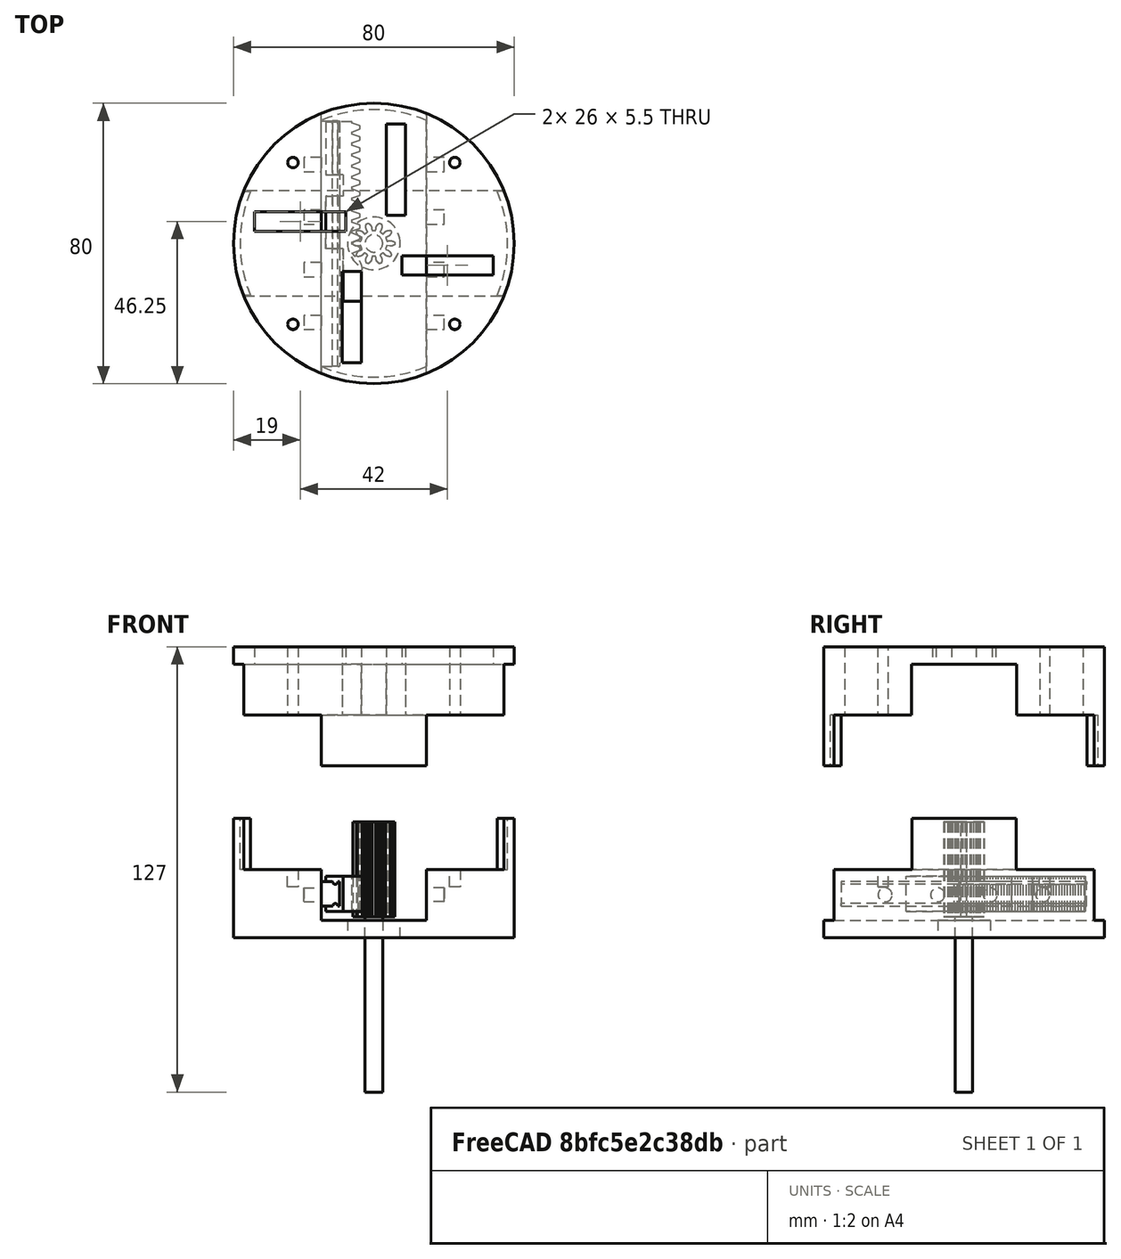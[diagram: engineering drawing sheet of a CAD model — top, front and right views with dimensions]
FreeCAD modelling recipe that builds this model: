
FCSTD DOCUMENT  (FreeCAD 1.1R20260414 (Git shallow))
Label: 2+2Jaw
License: All rights reserved
LicenseURL: https://en.wikipedia.org/wiki/All_rights_reserved
objects: Sketcher::SketchObject×17, PartDesign::Pocket×11, App::Link×7, App::Point×6, PartDesign::Pad×6, PartDesign::Body×5, Part::DatumPlane×2, PartDesign::FeaturePython×2, App::FeaturePython×1, Assembly::JointGroup×1, Assembly::AssemblyObject×1
note: 94 computed .brp shape members not serialized (recipe doc carries the construction recipe); baked Part::Feature solids carry a one-line shape summary decoded from their .brp

FEATURE [App::Point] Origin001
  Role = Origin
FEATURE [App::Point] Origin005  label="Origin006"
  Role = Origin
FEATURE [Sketcher::SketchObject] Sketch
  ArcFitTolerance = 1e-06
  AttachmentSupport = -> [Origin004]
  ExternalTypes = [0]
  FullyConstrained = true
  MakeInternals = false
  MapMode = 5
  _ExternalGeoVersion = 1
  sketch-geometry (2):
    g0: Circle CenterX=0 CenterY=0 CenterZ=0 NormalX=0 NormalY=0 NormalZ=1 AngleXU=0 Radius=40
    g1: Circle CenterX=0 CenterY=0 CenterZ=0 NormalX=0 NormalY=0 NormalZ=1 AngleXU=0 Radius=7.5
  constraints (4):
    c: Diameter(g0) = 80
    c: Coincident(g0,g-1)
    c: Diameter(g1) = 15
    c: Coincident(g1,g0)
FEATURE [PartDesign::Pad] Pad
  Direction = (0,0,1)
  Length = 34
  Length2 = 10
  Profile = -> Sketch
  ReferenceAxis = -> Sketch [N_Axis]
  Refine = true
  SideType = 0
  Suppressed = false
  Type = 0
  Type2 = 0
FEATURE [Part::DatumPlane] DatumPlane
  AttachmentSupport = -> [Origin004]
  MapMode = 5
  Placement = pos=(0,0,0) rot=(1,0,0;1.5708rad)
FEATURE [Sketcher::SketchObject] Sketch001
  ArcFitTolerance = 1e-06
  AttachmentSupport = -> [DatumPlane]
  ExternalGeometry = -> [Pad]
  ExternalTypes = [0,0,0]
  FullyConstrained = true
  MakeInternals = false
  MapMode = 5
  Placement = pos=(0,0,0) rot=(1,0,0;1.5708rad)
  _ExternalGeoVersion = 1
  sketch-geometry (5):
    g0: LineSegment StartX=-15 StartY=34 StartZ=0 EndX=-15 EndY=5 EndZ=0
    g1: LineSegment StartX=-15 StartY=5 StartZ=0 EndX=15 EndY=5 EndZ=0
    g2: LineSegment StartX=15 StartY=5 StartZ=0 EndX=15 EndY=34 EndZ=0
    g3: LineSegment StartX=-15 StartY=34 StartZ=0 EndX=0 EndY=34 EndZ=0
    g4: LineSegment StartX=0 StartY=34 StartZ=0 EndX=15 EndY=34 EndZ=0
  constraints (15):
    c: Coincident(g0,g1)
    c: Coincident(g1,g2)
    c: Vertical(g0)
    c: Vertical(g2)
    c: Horizontal(g1)
    c: Distance(g1,g-4) = 5
    c: Coincident(g0,g3)
    c: Horizontal(g3)
    c: Coincident(g3,g4)
    c: Horizontal(g4)
    c: PointOnObject(g3,g-2)
    c: Coincident(g4,g2)
    c: Equal(g3,g4)
    c: PointOnObject(g0,g-3)
    c: DistanceX(g1,g1) = 30
FEATURE [PartDesign::Pocket] Pocket
  BaseFeature = -> Pad
  Direction = (0,1,-2e-16)
  Length = 5
  Length2 = 5
  Profile = -> Sketch001
  ReferenceAxis = -> Sketch001 [N_Axis]
  Refine = true
  SideType = 2
  Suppressed = false
  Type = 1
  Type2 = 0
FEATURE [Sketcher::SketchObject] Sketch002
  ArcFitTolerance = 1e-06
  AttachmentSupport = -> [Pocket]
  ExternalGeometry = -> [Pocket]
  ExternalTypes = [0,0,0]
  FullyConstrained = true
  MakeInternals = false
  MapMode = 5
  Placement = pos=(0,0,34) rot=(0,0,1;0rad)
  _ExternalGeoVersion = 1
  sketch-geometry (16):
    g0: LineSegment StartX=35.1413 StartY=-14.85 StartZ=0 EndX=37.1413 EndY=-14.85 EndZ=0
    g1: LineSegment StartX=37.1413 StartY=14.85 StartZ=0 EndX=35.1413 EndY=14.85 EndZ=0
    g2: LineSegment [constr] StartX=37.1413 StartY=-14.85 StartZ=0 EndX=37.1413 EndY=0 EndZ=0
    g3: LineSegment [constr] StartX=37.1413 StartY=0 StartZ=0 EndX=37.1413 EndY=14.85 EndZ=0
    g4: ArcOfCircle CenterX=0 CenterY=0 CenterZ=0 NormalX=0 NormalY=0 NormalZ=1 AngleXU=0 Radius=38.1502 StartAngle=5.88337 EndAngle=6.683
    g5: LineSegment StartX=-35.1413 StartY=-14.85 StartZ=0 EndX=-37.1413 EndY=-14.85 EndZ=0
    g6: LineSegment StartX=-37.1413 StartY=14.85 StartZ=0 EndX=-35.1413 EndY=14.85 EndZ=0
    g7: LineSegment [constr] StartX=-37.1413 StartY=-14.85 StartZ=0 EndX=-37.1413 EndY=0 EndZ=0
    g8: LineSegment [constr] StartX=-37.1413 StartY=0 StartZ=0 EndX=-37.1413 EndY=14.85 EndZ=0
    g9: ArcOfCircle CenterX=0 CenterY=0 CenterZ=0 NormalX=0 NormalY=0 NormalZ=1 AngleXU=0 Radius=38.1502 StartAngle=2.74177 EndAngle=3.54141
    g10: LineSegment StartX=-37.1413 StartY=14.85 StartZ=0 EndX=-37.1413 EndY=40 EndZ=0
    g11: LineSegment StartX=-37.1413 StartY=40 StartZ=0 EndX=37.1413 EndY=40 EndZ=0
    g12: LineSegment StartX=-37.1413 StartY=-14.85 StartZ=0 EndX=-37.1413 EndY=-40 EndZ=0
    g13: LineSegment StartX=-37.1413 StartY=-40 StartZ=0 EndX=37.1413 EndY=-40 EndZ=0
    g14: LineSegment StartX=37.1413 StartY=-40 StartZ=0 EndX=37.1413 EndY=-14.85 EndZ=0
    g15: LineSegment StartX=37.1413 StartY=14.85 StartZ=0 EndX=37.1413 EndY=40 EndZ=0
  constraints (46):
    c: Horizontal(g0)
    c: Horizontal(g1)
    c: Coincident(g2,g0)
    c: PointOnObject(g2,g-1)
    c: Vertical(g2)
    c: Coincident(g3,g2)
    c: Coincident(g3,g1)
    c: Vertical(g3)
    c: Equal(g2,g3)
    c: PointOnObject(g1,g-3)
    c: Coincident(g4,g-3)
    c: Coincident(g4,g0)
    c: Coincident(g4,g1)
    c: Distance(g1,g1) = 2
    c: Horizontal(g5)
    c: Horizontal(g6)
    c: Coincident(g7,g5)
    c: Vertical(g7)
    c: Coincident(g8,g7)
    c: Coincident(g8,g6)
    c: Vertical(g8)
    c: Equal(g7,g8)
    c: Coincident(g9,g5)
    c: Coincident(g9,g6)
    c: Coincident(g9,g4)
    c: PointOnObject(g7,g-1)
    c: PointOnObject(g5,g-3)
    c: Equal(g7,g2)
    c: Distance(g5,g6) = 29.7
    c: Coincident(g6,g10)
    c: Vertical(g10)
    c: Coincident(g10,g11)
    c: Horizontal(g11)
    c: Coincident(g5,g12)
    c: Vertical(g12)
    c: Coincident(g12,g13)
    c: Horizontal(g13)
    c: Coincident(g13,g14)
    c: Coincident(g14,g0)
    c: Vertical(g14)
    c: Coincident(g15,g1)
    c: Coincident(g15,g11)
    c: Vertical(g15)
    c: Tangent(g13,g-3)
    c: Equal(g6,g1)
    c: Tangent(g11,g-3)
FEATURE [PartDesign::Pocket] Pocket001
  BaseFeature = -> Pocket
  Direction = (0,0,-1)
  Length = 14.5
  Length2 = 5
  Profile = -> Sketch002
  ReferenceAxis = -> Sketch002 [N_Axis]
  Refine = true
  SideType = 0
  Suppressed = false
  Type = 0
  Type2 = 0
FEATURE [Sketcher::SketchObject] Sketch003
  ArcFitTolerance = 1e-06
  AttachmentSupport = -> [Pocket001]
  ExternalGeometry = -> [Pocket001]
  ExternalTypes = [0,0,0,0]
  FullyConstrained = true
  MakeInternals = false
  MapMode = 5
  Placement = pos=(0,0,19.5) rot=(0,0,1;0rad)
  _ExternalGeoVersion = 1
  sketch-geometry (20):
    g0: Circle CenterX=-23.0923 CenterY=22.9991 CenterZ=0 NormalX=0 NormalY=0 NormalZ=1 AngleXU=0 Radius=1.5
    g1: ArcOfCircle [constr] CenterX=-45.3233 CenterY=45.1404 CenterZ=0 NormalX=0 NormalY=0 NormalZ=1 AngleXU=0 Radius=31.376 StartAngle=4.97621 EndAngle=6.02341
    g2: LineSegment [constr] StartX=-37.1413 StartY=14.85 StartZ=0 EndX=-23.0923 EndY=22.9991 EndZ=0
    g3: LineSegment [constr] StartX=-23.0923 StartY=22.9991 StartZ=0 EndX=-15 EndY=37.081 EndZ=0
    g4: LineSegment [constr] StartX=-37.1413 StartY=14.85 StartZ=0 EndX=-15 EndY=37.081 EndZ=0
    g5: ArcOfCircle [constr] CenterX=45.3233 CenterY=45.1404 CenterZ=0 NormalX=0 NormalY=0 NormalZ=1 AngleXU=0 Radius=31.376 StartAngle=3.40137 EndAngle=4.44857
    g6: ArcOfCircle [constr] CenterX=-45.3233 CenterY=-45.1404 CenterZ=0 NormalX=0 NormalY=0 NormalZ=1 AngleXU=0 Radius=31.376 StartAngle=0.259778 EndAngle=1.30698
    g7: ArcOfCircle [constr] CenterX=45.3233 CenterY=-45.1404 CenterZ=0 NormalX=0 NormalY=0 NormalZ=1 AngleXU=0 Radius=31.376 StartAngle=1.83462 EndAngle=2.88181
    g8: LineSegment [constr] StartX=-37.1413 StartY=-14.85 StartZ=0 EndX=-23.0923 EndY=-22.9991 EndZ=0
    g9: LineSegment [constr] StartX=-23.0923 StartY=-22.9991 StartZ=0 EndX=-15 EndY=-37.081 EndZ=0
    g10: LineSegment [constr] StartX=-15 StartY=-37.081 StartZ=0 EndX=-37.1413 EndY=-14.85 EndZ=0
    g11: LineSegment [constr] StartX=15 StartY=-37.081 StartZ=0 EndX=37.1413 EndY=-14.85 EndZ=0
    g12: LineSegment [constr] StartX=37.1413 StartY=-14.85 StartZ=0 EndX=23.0923 EndY=-22.9991 EndZ=0
    g13: LineSegment [constr] StartX=23.0923 StartY=-22.9991 StartZ=0 EndX=15 EndY=-37.081 EndZ=0
    g14: LineSegment [constr] StartX=15 StartY=37.081 StartZ=0 EndX=23.0923 EndY=22.9991 EndZ=0
    g15: LineSegment [constr] StartX=23.0923 StartY=22.9991 StartZ=0 EndX=37.1413 EndY=14.85 EndZ=0
    g16: LineSegment [constr] StartX=37.1413 StartY=14.85 StartZ=0 EndX=15 EndY=37.081 EndZ=0
    g17: Circle CenterX=23.0923 CenterY=22.9991 CenterZ=0 NormalX=0 NormalY=0 NormalZ=1 AngleXU=0 Radius=1.5
    g18: Circle CenterX=23.0923 CenterY=-22.9991 CenterZ=0 NormalX=0 NormalY=0 NormalZ=1 AngleXU=0 Radius=1.5
    g19: Circle CenterX=-23.0923 CenterY=-22.9991 CenterZ=0 NormalX=0 NormalY=0 NormalZ=1 AngleXU=0 Radius=1.5
  constraints (48):
    c: Diameter(g0) = 3
    c: Coincident(g1,g-6)
    c: Coincident(g1,g-6)
    c: PointOnObject(g0,g1)
    c: Coincident(g1,g2)
    c: Coincident(g2,g3)
    c: Coincident(g3,g1)
    c: Equal(g3,g2)
    c: Coincident(g2,g0)
    c: Coincident(g4,g1)
    c: Coincident(g4,g1)
    c: Angle(g2,g4) = 0.261799
    c: Coincident(g5,g-3)
    c: Coincident(g5,g-3)
    c: Coincident(g6,g-5)
    c: Coincident(g6,g-5)
    c: Coincident(g7,g-4)
    c: Coincident(g7,g-4)
    c: Coincident(g6,g8)
    c: Coincident(g8,g9)
    c: Coincident(g9,g6)
    c: Coincident(g9,g10)
    c: Coincident(g10,g8)
    c: Coincident(g7,g11)
    c: Coincident(g11,g12)
    c: Coincident(g12,g13)
    c: Coincident(g13,g11)
    c: Coincident(g5,g14)
    c: Coincident(g14,g15)
    c: Coincident(g15,g5)
    c: Coincident(g15,g16)
    c: Coincident(g16,g14)
    c: Equal(g8,g9)
    c: Equal(g15,g14)
    c: Equal(g12,g13)
    c: PointOnObject(g8,g6)
    c: PointOnObject(g12,g7)
    c: Coincident(g11,g7)
    c: PointOnObject(g14,g5)
    c: Angle(g10,g8) = 0.261799
    c: Angle(g12,g11) = 0.261799
    c: Angle(g16,g15) = 0.261799
    c: Coincident(g17,g14)
    c: Coincident(g18,g12)
    c: Coincident(g19,g8)
    c: Equal(g0,g17)
    c: Equal(g0,g19)
    c: Equal(g0,g18)
FEATURE [PartDesign::Pocket] Pocket002
  BaseFeature = -> Pocket001
  Direction = (0,0,-1)
  Length = 5
  Length2 = 5
  Profile = -> Sketch003
  ReferenceAxis = -> Sketch003 [N_Axis]
  Refine = true
  SideType = 0
  Suppressed = false
  Type = 0
  Type2 = 0
FEATURE [Part::DatumPlane] DatumPlane001
  AttachmentSupport = -> [Origin006]
  MapMode = 5
  Placement = pos=(0,0,0) rot=(1,0,0;1.5708rad)
FEATURE [App::Point] Origin007  label="Origin009"
  Role = Origin
FEATURE [Sketcher::SketchObject] Sketch004
  ArcFitTolerance = 1e-06
  AttachmentSupport = -> [Origin006]
  ExternalTypes = [0]
  FullyConstrained = true
  MakeInternals = false
  MapMode = 5
  _ExternalGeoVersion = 1
  sketch-geometry (1):
    g0: Circle CenterX=0 CenterY=0 CenterZ=0 NormalX=0 NormalY=0 NormalZ=1 AngleXU=0 Radius=40
  constraints (2):
    c: Diameter(g0) = 80
    c: Coincident(g0,g-1)
FEATURE [PartDesign::Pad] Pad001
  Direction = (0,0,1)
  Length = 34
  Length2 = 10
  Profile = -> Sketch004
  ReferenceAxis = -> Sketch004 [N_Axis]
  Refine = true
  SideType = 0
  Suppressed = false
  Type = 0
  Type2 = 0
FEATURE [Sketcher::SketchObject] Sketch005
  ArcFitTolerance = 1e-06
  AttachmentSupport = -> [DatumPlane001]
  ExternalGeometry = -> [Pad001]
  ExternalTypes = [0,0,0]
  FullyConstrained = true
  MakeInternals = false
  MapMode = 5
  Placement = pos=(0,0,0) rot=(1,0,0;1.5708rad)
  _ExternalGeoVersion = 1
  sketch-geometry (5):
    g0: LineSegment StartX=-15 StartY=34 StartZ=0 EndX=-15 EndY=5 EndZ=0
    g1: LineSegment StartX=-15 StartY=5 StartZ=0 EndX=15 EndY=5 EndZ=0
    g2: LineSegment StartX=15 StartY=5 StartZ=0 EndX=15 EndY=34 EndZ=0
    g3: LineSegment StartX=-15 StartY=34 StartZ=0 EndX=0 EndY=34 EndZ=0
    g4: LineSegment StartX=0 StartY=34 StartZ=0 EndX=15 EndY=34 EndZ=0
  constraints (15):
    c: Coincident(g0,g1)
    c: Coincident(g1,g2)
    c: Vertical(g0)
    c: Vertical(g2)
    c: Horizontal(g1)
    c: Distance(g1,g-4) = 5
    c: Coincident(g0,g3)
    c: Horizontal(g3)
    c: Coincident(g3,g4)
    c: Horizontal(g4)
    c: PointOnObject(g3,g-2)
    c: Coincident(g4,g2)
    c: Equal(g3,g4)
    c: PointOnObject(g0,g-3)
    c: DistanceX(g1,g1) = 30
FEATURE [PartDesign::Pocket] Pocket003
  BaseFeature = -> Pad001
  Direction = (0,1,-2e-16)
  Length = 5
  Length2 = 5
  Profile = -> Sketch005
  ReferenceAxis = -> Sketch005 [N_Axis]
  Refine = true
  SideType = 2
  Suppressed = false
  Type = 1
  Type2 = 0
FEATURE [Sketcher::SketchObject] Sketch006
  ArcFitTolerance = 1e-06
  AttachmentSupport = -> [Pocket003]
  ExternalGeometry = -> [Pocket003]
  ExternalTypes = [0,0,0]
  FullyConstrained = true
  MakeInternals = false
  MapMode = 5
  Placement = pos=(0,0,34) rot=(0,0,1;0rad)
  _ExternalGeoVersion = 1
  sketch-geometry (16):
    g0: LineSegment StartX=35.081 StartY=-15 StartZ=0 EndX=37.081 EndY=-15 EndZ=0
    g1: LineSegment StartX=37.081 StartY=15 StartZ=0 EndX=35.081 EndY=15 EndZ=0
    g2: LineSegment [constr] StartX=37.081 StartY=-15 StartZ=0 EndX=37.081 EndY=0 EndZ=0
    g3: LineSegment [constr] StartX=37.081 StartY=0 StartZ=0 EndX=37.081 EndY=15 EndZ=0
    g4: ArcOfCircle CenterX=0 CenterY=0 CenterZ=0 NormalX=0 NormalY=0 NormalZ=1 AngleXU=0 Radius=38.1533 StartAngle=5.87913 EndAngle=6.68724
    g5: LineSegment StartX=-35.081 StartY=-15 StartZ=0 EndX=-37.081 EndY=-15 EndZ=0
    g6: LineSegment StartX=-37.081 StartY=15 StartZ=0 EndX=-35.081 EndY=15 EndZ=0
    g7: LineSegment [constr] StartX=-37.081 StartY=-15 StartZ=0 EndX=-37.081 EndY=0 EndZ=0
    g8: LineSegment [constr] StartX=-37.081 StartY=0 StartZ=0 EndX=-37.081 EndY=15 EndZ=0
    g9: ArcOfCircle CenterX=0 CenterY=0 CenterZ=0 NormalX=0 NormalY=0 NormalZ=1 AngleXU=0 Radius=38.1533 StartAngle=2.73754 EndAngle=3.54565
    g10: LineSegment StartX=-37.081 StartY=15 StartZ=0 EndX=-37.081 EndY=40 EndZ=0
    g11: LineSegment StartX=-37.081 StartY=40 StartZ=0 EndX=37.081 EndY=40 EndZ=0
    g12: LineSegment StartX=-37.081 StartY=-15 StartZ=0 EndX=-37.081 EndY=-40 EndZ=0
    g13: LineSegment StartX=-37.081 StartY=-40 StartZ=0 EndX=37.081 EndY=-40 EndZ=0
    g14: LineSegment StartX=37.081 StartY=-40 StartZ=0 EndX=37.081 EndY=-15 EndZ=0
    g15: LineSegment StartX=37.081 StartY=15 StartZ=0 EndX=37.081 EndY=40 EndZ=0
  constraints (46):
    c: Horizontal(g0)
    c: Horizontal(g1)
    c: Coincident(g2,g0)
    c: PointOnObject(g2,g-1)
    c: Vertical(g2)
    c: Coincident(g3,g2)
    c: Coincident(g3,g1)
    c: Vertical(g3)
    c: Equal(g2,g3)
    c: PointOnObject(g1,g-3)
    c: Coincident(g4,g-3)
    c: Coincident(g4,g0)
    c: Coincident(g4,g1)
    c: Distance(g1,g1) = 2
    c: Horizontal(g5)
    c: Horizontal(g6)
    c: Coincident(g7,g5)
    c: Vertical(g7)
    c: Coincident(g8,g7)
    c: Coincident(g8,g6)
    c: Vertical(g8)
    c: Equal(g7,g8)
    c: Coincident(g9,g5)
    c: Coincident(g9,g6)
    c: Coincident(g9,g4)
    c: PointOnObject(g7,g-1)
    c: PointOnObject(g5,g-3)
    c: Equal(g7,g2)
    c: Distance(g5,g6) = 30
    c: Coincident(g6,g10)
    c: Vertical(g10)
    c: Coincident(g10,g11)
    c: Horizontal(g11)
    c: Coincident(g5,g12)
    c: Vertical(g12)
    c: Coincident(g12,g13)
    c: Horizontal(g13)
    c: Coincident(g13,g14)
    c: Coincident(g14,g0)
    c: Vertical(g14)
    c: Coincident(g15,g1)
    c: Coincident(g15,g11)
    c: Vertical(g15)
    c: Tangent(g13,g-3)
    c: Equal(g6,g1)
    c: Tangent(g11,g-3)
FEATURE [PartDesign::Pocket] Pocket004
  BaseFeature = -> Pocket003
  Direction = (0,0,-1)
  Length = 14.5
  Length2 = 5
  Profile = -> Sketch006
  ReferenceAxis = -> Sketch006 [N_Axis]
  Refine = true
  SideType = 0
  Suppressed = false
  Type = 0
  Type2 = 0
FEATURE [Sketcher::SketchObject] Sketch007
  ArcFitTolerance = 1e-06
  AttachmentSupport = -> [Pocket004]
  ExternalGeometry = -> [Pocket004]
  ExternalTypes = [0,0,0,0]
  FullyConstrained = true
  MakeInternals = false
  MapMode = 5
  Placement = pos=(0,0,19.5) rot=(0,0,1;0rad)
  _ExternalGeoVersion = 1
  sketch-geometry (20):
    g0: Circle CenterX=-23.0822 CenterY=23.0822 CenterZ=0 NormalX=0 NormalY=0 NormalZ=1 AngleXU=0 Radius=1.5
    g1: ArcOfCircle [constr] CenterX=-45.1632 CenterY=45.1632 CenterZ=0 NormalX=0 NormalY=0 NormalZ=1 AngleXU=0 Radius=31.2272 StartAngle=4.97419 EndAngle=6.02139
    g2: LineSegment [constr] StartX=-37.081 StartY=15 StartZ=0 EndX=-23.0822 EndY=23.0822 EndZ=0
    g3: LineSegment [constr] StartX=-23.0822 StartY=23.0822 StartZ=0 EndX=-15 EndY=37.081 EndZ=0
    g4: LineSegment [constr] StartX=-37.081 StartY=15 StartZ=0 EndX=-15 EndY=37.081 EndZ=0
    g5: ArcOfCircle [constr] CenterX=45.1632 CenterY=45.1632 CenterZ=0 NormalX=0 NormalY=0 NormalZ=1 AngleXU=0 Radius=31.2272 StartAngle=3.40339 EndAngle=4.45059
    g6: ArcOfCircle [constr] CenterX=-45.1632 CenterY=-45.1632 CenterZ=0 NormalX=0 NormalY=0 NormalZ=1 AngleXU=0 Radius=31.2272 StartAngle=0.261799 EndAngle=1.309
    g7: ArcOfCircle [constr] CenterX=45.1632 CenterY=-45.1632 CenterZ=0 NormalX=0 NormalY=0 NormalZ=1 AngleXU=0 Radius=31.2272 StartAngle=1.8326 EndAngle=2.87979
    g8: LineSegment [constr] StartX=-37.081 StartY=-15 StartZ=0 EndX=-23.0822 EndY=-23.0822 EndZ=0
    g9: LineSegment [constr] StartX=-23.0822 StartY=-23.0822 StartZ=0 EndX=-15 EndY=-37.081 EndZ=0
    g10: LineSegment [constr] StartX=-15 StartY=-37.081 StartZ=0 EndX=-37.081 EndY=-15 EndZ=0
    g11: LineSegment [constr] StartX=15 StartY=-37.081 StartZ=0 EndX=37.081 EndY=-15 EndZ=0
    g12: LineSegment [constr] StartX=37.081 StartY=-15 StartZ=0 EndX=23.0822 EndY=-23.0822 EndZ=0
    g13: LineSegment [constr] StartX=23.0822 StartY=-23.0822 StartZ=0 EndX=15 EndY=-37.081 EndZ=0
    g14: LineSegment [constr] StartX=15 StartY=37.081 StartZ=0 EndX=23.0822 EndY=23.0822 EndZ=0
    g15: LineSegment [constr] StartX=23.0822 StartY=23.0822 StartZ=0 EndX=37.081 EndY=15 EndZ=0
    g16: LineSegment [constr] StartX=37.081 StartY=15 StartZ=0 EndX=15 EndY=37.081 EndZ=0
    g17: Circle CenterX=23.0822 CenterY=23.0822 CenterZ=0 NormalX=0 NormalY=0 NormalZ=1 AngleXU=0 Radius=1.5
    g18: Circle CenterX=23.0822 CenterY=-23.0822 CenterZ=0 NormalX=0 NormalY=0 NormalZ=1 AngleXU=0 Radius=1.5
    g19: Circle CenterX=-23.0822 CenterY=-23.0822 CenterZ=0 NormalX=0 NormalY=0 NormalZ=1 AngleXU=0 Radius=1.5
  constraints (48):
    c: Diameter(g0) = 3
    c: Coincident(g1,g-6)
    c: Coincident(g1,g-6)
    c: PointOnObject(g0,g1)
    c: Coincident(g1,g2)
    c: Coincident(g2,g3)
    c: Coincident(g3,g1)
    c: Equal(g3,g2)
    c: Coincident(g2,g0)
    c: Coincident(g4,g1)
    c: Coincident(g4,g1)
    c: Angle(g2,g4) = 0.261799
    c: Coincident(g5,g-3)
    c: Coincident(g5,g-3)
    c: Coincident(g6,g-5)
    c: Coincident(g6,g-5)
    c: Coincident(g7,g-4)
    c: Coincident(g7,g-4)
    c: Coincident(g6,g8)
    c: Coincident(g8,g9)
    c: Coincident(g9,g6)
    c: Coincident(g9,g10)
    c: Coincident(g10,g8)
    c: Coincident(g7,g11)
    c: Coincident(g11,g12)
    c: Coincident(g12,g13)
    c: Coincident(g13,g11)
    c: Coincident(g5,g14)
    c: Coincident(g14,g15)
    c: Coincident(g15,g5)
    c: Coincident(g15,g16)
    c: Coincident(g16,g14)
    c: Equal(g8,g9)
    c: Equal(g15,g14)
    c: Equal(g12,g13)
    c: PointOnObject(g8,g6)
    c: PointOnObject(g12,g7)
    c: Coincident(g11,g7)
    c: PointOnObject(g14,g5)
    c: Angle(g10,g8) = 0.261799
    c: Angle(g12,g11) = 0.261799
    c: Angle(g16,g15) = 0.261799
    c: Coincident(g17,g14)
    c: Coincident(g18,g12)
    c: Coincident(g19,g8)
    c: Equal(g0,g17)
    c: Equal(g0,g19)
    c: Equal(g0,g18)
FEATURE [PartDesign::Pocket] Pocket005
  BaseFeature = -> Pocket004
  Direction = (0,0,-1)
  Length = 5
  Length2 = 5
  Profile = -> Sketch007
  ReferenceAxis = -> Sketch007 [N_Axis]
  Refine = true
  SideType = 0
  Suppressed = false
  Type = 1
  Type2 = 0
FEATURE [App::Point] Origin009  label="Origin011"
  Role = Origin
FEATURE [App::Point] Origin011  label="Origin013"
  Role = Origin
FEATURE [PartDesign::FeaturePython] InvoluteGear  # WARN: FeaturePython — macro-defined, semantics opaque (R4)
  AttacherType = Attacher::AttachEngine3D
  Suppressed = false
  addendum_diameter = 12
  angular_backlash = 0
  axle_hole = false
  axle_holesize = 10
  backlash = 0
  clearance = 0.25
  double_helix = false
  head = 0
  head_fillet = 0
  height = 27
  helix_angle = 0
  module = 1
  num_teeth = 10
  numpoints = 20
  offset_hole = false
  offset_holeoffset = 10
  offset_holesize = 10
  pitch_diameter = 10
  pressure_angle = 20
  properties_from_tool = false
  reversed_backlash = false
  root_diameter = 7.5
  root_fillet = 0
  shift = 0
  simple = false
  transverse_pitch = 3.14159
  traverse_module = 1
  undercut = false
  version = 1.3.0
  expr: angular_backlash = backlash / pitch_diameter * 360 ° / pi
FEATURE [Sketcher::SketchObject] Sketch008
  ArcFitTolerance = 1e-06
  AttachmentSupport = -> [InvoluteGear]
  ExternalTypes = [0]
  FullyConstrained = true
  MakeInternals = false
  MapMode = 5
  Placement = pos=(0,0,27) rot=(0,0,1;0rad)
  _ExternalGeoVersion = 1
  sketch-geometry (1):
    g0: Circle CenterX=0 CenterY=0 CenterZ=0 NormalX=0 NormalY=0 NormalZ=1 AngleXU=0 Radius=2.5
  constraints (2):
    c: Diameter(g0) = 5
    c: Coincident(g0,g-1)
FEATURE [PartDesign::Pad] Pad002
  BaseFeature = -> InvoluteGear
  Direction = (0,0,1)
  Length = 50
  Length2 = 10
  Profile = -> Sketch008
  ReferenceAxis = -> Sketch008 [N_Axis]
  Refine = true
  SideType = 0
  Suppressed = false
  Type = 0
  Type2 = 0
FEATURE [PartDesign::Body] Body003  label="Shaft"
  AllowCompound = false
  Group = -> [InvoluteGear,Sketch008,Pad002]
  Origin = -> Origin010
  Placement = pos=(0,4e-15,33) rot=(1,0,0;3.14159rad)
  Tip = -> Pad002
FEATURE [PartDesign::FeaturePython] InvoluteRack  # WARN: FeaturePython — macro-defined, semantics opaque (R4)
  AttacherType = Attacher::AttachEngine3D
  Suppressed = false
  add_endings = true
  clearance = 0.25
  double_helix = false
  head = 0
  head_fillet = 0
  height = 10
  helix_angle = 0
  module = 1
  num_teeth = 12
  pressure_angle = 20
  properties_from_tool = false
  root_fillet = 0
  simplified = false
  thickness = 1
  transverse_pitch = 3.14159
  version = 1.3.0
FEATURE [Sketcher::SketchObject] Sketch009
  ArcFitTolerance = 1e-06
  AttachmentSupport = -> [InvoluteRack]
  ExternalGeometry = -> [InvoluteRack]
  ExternalTypes = [0,0,0]
  FullyConstrained = true
  MakeInternals = false
  MapMode = 5
  Placement = pos=(0,0,0) rot=(1,0,0;3.14159rad)
  _ExternalGeoVersion = 1
  sketch-geometry (10):
    g0: ArcOfCircle CenterX=2.74624 CenterY=-1.76464 CenterZ=0 NormalX=0 NormalY=0 NormalZ=1 AngleXU=0 Radius=5 StartAngle=2.2143 EndAngle=3.10281
    g1: LineSegment StartX=-3.75 StartY=-36.1283 StartZ=0 EndX=-3.75 EndY=15 EndZ=0
    g2: LineSegment StartX=-3.75 StartY=15 StartZ=0 EndX=1.74624 EndY=15 EndZ=0
    g3: LineSegment StartX=1.74624 StartY=15 StartZ=0 EndX=1.74624 EndY=6.23536 EndZ=0
    g4: ArcOfCircle CenterX=-3.25376 CenterY=6.23536 CenterZ=0 NormalX=0 NormalY=0 NormalZ=1 AngleXU=0 Radius=5 StartAngle=5.35589 EndAngle=6.28319
    g5: LineSegment [constr] StartX=2.74624 StartY=-1.76464 StartZ=0 EndX=2.74624 EndY=15 EndZ=0
    g6: LineSegment [constr] StartX=1.74624 StartY=15 StartZ=0 EndX=2.74624 EndY=15 EndZ=0
    g7: LineSegment [constr] StartX=-2.25 StartY=-1.5708 StartZ=0 EndX=-1.25 EndY=-1.5708 EndZ=0
    g8: LineSegment StartX=-2.25 StartY=-1.5708 StartZ=0 EndX=-2.25 EndY=-36.1283 EndZ=0
    g9: LineSegment StartX=-2.25 StartY=-36.1283 StartZ=0 EndX=-3.75 EndY=-36.1283 EndZ=0
  constraints (27):
    c: Radius(g0) = 5
    c: Vertical(g1)
    c: Coincident(g1,g2)
    c: Horizontal(g2)
    c: Coincident(g2,g3)
    c: Vertical(g3)
    c: Coincident(g5,g0)
    c: Vertical(g5)
    c: Coincident(g6,g2)
    c: Coincident(g6,g5)
    c: Horizontal(g6)
    c: Tangent(g4,g0) = 1.5708
    c: Tangent(g4,g3) = 1.5708
    c: PointOnObject(g-3,g0)
    c: Distance(g-1,g2) = 15
    c: Equal(g4,g0)
    c: Coincident(g7,g0)
    c: Symmetric(g-4,g-4,g7)
    c: Horizontal(g7)
    c: Distance(g3,g5) = 1
    c: Coincident(g8,g0)
    c: Coincident(g8,g-5)
    c: Vertical(g8)
    c: Coincident(g9,g8)
    c: Coincident(g9,g1)
    c: Horizontal(g9)
    c: Distance(g9,g9) = 1.5
FEATURE [App::Point] Origin013  label="Origin016"
  Role = Origin
FEATURE [Sketcher::SketchObject] Sketch012
  ArcFitTolerance = 1e-06
  AttachmentSupport = -> [Origin012]
  ExternalTypes = [0]
  FullyConstrained = true
  MakeInternals = false
  MapMode = 5
  _ExternalGeoVersion = 1
  sketch-geometry (4):
    g0: LineSegment StartX=0 StartY=0 StartZ=0 EndX=70 EndY=0 EndZ=0
    g1: LineSegment StartX=70 StartY=0 StartZ=0 EndX=70 EndY=7 EndZ=0
    g2: LineSegment StartX=70 StartY=7 StartZ=0 EndX=0 EndY=7 EndZ=0
    g3: LineSegment StartX=0 StartY=7 StartZ=0 EndX=0 EndY=0 EndZ=0
  constraints (11):
    c: Coincident(g0,g1)
    c: Coincident(g1,g2)
    c: Coincident(g2,g3)
    c: Coincident(g3,g0)
    c: Horizontal(g0)
    c: Horizontal(g2)
    c: Vertical(g1)
    c: Vertical(g3)
    c: Distance(g1,g3) = 70
    c: Distance(g0,g2) = 7
    c: Coincident(g0,g-1)
FEATURE [PartDesign::Pad] Pad005
  Direction = (0,0,1)
  Length = 5.25
  Length2 = 10
  Profile = -> Sketch012
  ReferenceAxis = -> Sketch012 [N_Axis]
  Refine = true
  SideType = 0
  Suppressed = false
  Type = 0
  Type2 = 0
FEATURE [Sketcher::SketchObject] Sketch013
  ArcFitTolerance = 1e-06
  AttachmentSupport = -> [Pad005]
  ExternalGeometry = -> [Pad005]
  ExternalTypes = [0,0,0]
  FullyConstrained = true
  MakeInternals = false
  MapMode = 5
  Placement = pos=(0,0,0) rot=(0.57735,-0.57735,-0.57735;2.0944rad)
  _ExternalGeoVersion = 1
  sketch-geometry (5):
    g0: LineSegment StartX=-7 StartY=4.75 StartZ=0 EndX=-7 EndY=3.25 EndZ=0
    g1: ArcOfCircle CenterX=-7 CenterY=4 CenterZ=0 NormalX=0 NormalY=0 NormalZ=1 AngleXU=0 Radius=0.75 StartAngle=4.71239 EndAngle=7.85398
    g2: LineSegment StartX=-2.6e-15 StartY=4.75 StartZ=0 EndX=-2.6e-15 EndY=3.25 EndZ=0
    g3: ArcOfCircle CenterX=-1.20374e-05 CenterY=4 CenterZ=0 NormalX=0 NormalY=0 NormalZ=1 AngleXU=0 Radius=0.75 StartAngle=1.57078 EndAngle=4.71241
    g4: LineSegment [constr] StartX=-2.6e-15 StartY=4.75 StartZ=0 EndX=-7 EndY=4.75 EndZ=0
  constraints (16):
    c: PointOnObject(g0,g-4)
    c: PointOnObject(g2,g-5)
    c: Coincident(g4,g2)
    c: Coincident(g4,g0)
    c: Horizontal(g4)
    c: Tangent(g4,g3)
    c: Coincident(g1,g0)
    c: Radius(g1) = 0.75
    c: Distance(g-3,g4) = 0.5
    c: Coincident(g1,g0)
    c: Coincident(g2,g3)
    c: Equal(g1,g3)
    c: Vertical(g0)
    c: PointOnObject(g1,g0)
    c: Vertical(g2)
    c: Coincident(g3,g2)
FEATURE [PartDesign::Pocket] Pocket007
  BaseFeature = -> Pad005
  Direction = (1,0,0)
  Length = 5
  Length2 = 5
  Profile = -> Sketch013
  ReferenceAxis = -> Sketch013 [N_Axis]
  Refine = true
  SideType = 0
  Suppressed = false
  Type = 3
  Type2 = 0
  UpToFace = -> Pad005 [Face2]
FEATURE [PartDesign::Body] Body004  label="Rail"
  AllowCompound = false
  Group = -> [Sketch012,Pad005,Sketch013,Pocket007]
  Origin = -> Origin012
  Placement = pos=(-15,-35,9) rot=(0.57735,0.57735,0.57735;2.0944rad)
  Tip = -> Pocket007
FEATURE [PartDesign::Pad] Pad006
  BaseFeature = -> InvoluteRack
  Direction = (0,0,-1)
  Length = 10
  Length2 = 10
  Profile = -> Sketch009
  ReferenceAxis = -> Sketch009 [N_Axis]
  Refine = true
  SideType = 0
  Suppressed = false
  Type = 3
  Type2 = 0
  UpToFace = -> InvoluteRack [Face54]
FEATURE [Sketcher::SketchObject] Sketch010
  ArcFitTolerance = 1e-06
  AttachmentSupport = -> [Pad006]
  ExternalGeometry = -> [Pad006]
  ExternalTypes = [0]
  FullyConstrained = true
  MakeInternals = false
  MapMode = 5
  Placement = pos=(-3.75,0,0) rot=(0.57735,-0.57735,-0.57735;2.0944rad)
  _ExternalGeoVersion = 1
  sketch-geometry (8):
    g0: LineSegment StartX=-36.1283 StartY=10 StartZ=0 EndX=-36.1283 EndY=0 EndZ=0
    g1: LineSegment StartX=-36.1283 StartY=0 StartZ=0 EndX=-21.1283 EndY=0 EndZ=0
    g2: LineSegment StartX=-21.1283 StartY=0 StartZ=0 EndX=-21.1283 EndY=10 EndZ=0
    g3: LineSegment StartX=-21.1283 StartY=10 StartZ=0 EndX=-36.1283 EndY=10 EndZ=0
    g4: LineSegment StartX=0 StartY=0 StartZ=0 EndX=0 EndY=10 EndZ=0
    g5: LineSegment StartX=0 StartY=10 StartZ=0 EndX=-15 EndY=10 EndZ=0
    g6: LineSegment StartX=-15 StartY=10 StartZ=0 EndX=-15 EndY=0 EndZ=0
    g7: LineSegment StartX=-15 StartY=0 StartZ=0 EndX=0 EndY=0 EndZ=0
  constraints (22):
    c: Coincident(g0,g1)
    c: Coincident(g1,g2)
    c: Coincident(g2,g3)
    c: Coincident(g3,g0)
    c: Vertical(g0)
    c: Vertical(g2)
    c: Horizontal(g1)
    c: Horizontal(g3)
    c: Distance(g0,g2) = 15
    c: PointOnObject(g1,g-1)
    c: Coincident(g4,g5)
    c: Coincident(g5,g6)
    c: Coincident(g6,g7)
    c: Coincident(g7,g4)
    c: Vertical(g4)
    c: Vertical(g6)
    c: Horizontal(g5)
    c: Horizontal(g7)
    c: Distance(g4,g6) = 15
    c: Coincident(g4,g-1)
    c: Coincident(g0,g-3)
    c: PointOnObject(g5,g-3)
FEATURE [PartDesign::Pad] Pad007
  BaseFeature = -> Pad006
  Direction = (-1,0,0)
  Length = 5
  Length2 = 10
  Profile = -> Sketch010
  ReferenceAxis = -> Sketch010 [N_Axis]
  Refine = true
  SideType = 0
  Suppressed = false
  Type = 0
  Type2 = 0
FEATURE [Sketcher::SketchObject] Sketch011
  ArcFitTolerance = 1e-06
  AttachmentSupport = -> [Pad007]
  ExternalTypes = [0,0]
  FullyConstrained = true
  MakeInternals = false
  MapMode = 5
  Placement = pos=(-3.22e-14,36.1283,0) rot=(0,0.707107,0.707107;3.14159rad)
  _ExternalGeoVersion = 1
  sketch-geometry (14):
    g0: LineSegment StartX=8.75 StartY=1.5 StartZ=0 EndX=6.75 EndY=1.5 EndZ=0
    g1: LineSegment StartX=5.25 StartY=1.5 StartZ=0 EndX=4.75 EndY=1.5 EndZ=0
    g2: LineSegment StartX=4.75 StartY=1.5 StartZ=0 EndX=4.75 EndY=8.5 EndZ=0
    g3: LineSegment StartX=4.75 StartY=8.5 StartZ=0 EndX=5.25 EndY=8.5 EndZ=0
    g4: LineSegment StartX=6.75 StartY=8.5 StartZ=0 EndX=8.75 EndY=8.5 EndZ=0
    g5: LineSegment StartX=8.75 StartY=8.5 StartZ=0 EndX=8.75 EndY=1.5 EndZ=0
    g6: ArcOfCircle CenterX=6 CenterY=1.5 CenterZ=0 NormalX=0 NormalY=0 NormalZ=1 AngleXU=0 Radius=0.75 StartAngle=-1.8e-15 EndAngle=3.14159
    g7: ArcOfCircle CenterX=6 CenterY=8.5 CenterZ=0 NormalX=0 NormalY=0 NormalZ=1 AngleXU=0 Radius=0.75 StartAngle=3.14159 EndAngle=6.28318
    g8: LineSegment [constr] StartX=5.25 StartY=1.5 StartZ=0 EndX=5.25 EndY=8.5 EndZ=0
    g9: LineSegment [constr] StartX=6.75 StartY=8.5 StartZ=0 EndX=6.75 EndY=1.5 EndZ=0
    g10: LineSegment [constr] StartX=8.75 StartY=8.5 StartZ=0 EndX=8.75 EndY=10 EndZ=0
    g11: LineSegment [constr] StartX=8.75 StartY=1.5 StartZ=0 EndX=8.75 EndY=0 EndZ=0
    g12: LineSegment [constr] StartX=5.25 StartY=1.5 StartZ=0 EndX=6.75 EndY=1.5 EndZ=0
    g13: LineSegment [constr] StartX=5.25 StartY=8.5 StartZ=0 EndX=6.75 EndY=8.5 EndZ=0
  constraints (38):
    c: PointOnObject(g0,g-3)
    c: Horizontal(g0)
    c: Horizontal(g1)
    c: Coincident(g2,g1)
    c: Vertical(g2)
    c: Coincident(g3,g2)
    c: Horizontal(g3)
    c: PointOnObject(g4,g-3)
    c: Horizontal(g4)
    c: Coincident(g5,g4)
    c: Coincident(g5,g0)
    c: Coincident(g6,g1)
    c: Coincident(g6,g0)
    c: Coincident(g7,g3)
    c: Coincident(g7,g4)
    c: Equal(g7,g6)
    c: Coincident(g8,g1)
    c: Coincident(g8,g3)
    c: Vertical(g8)
    c: Coincident(g9,g4)
    c: Coincident(g9,g0)
    c: Vertical(g9)
    c: Coincident(g10,g4)
    c: Coincident(g10,g-3)
    c: Coincident(g11,g0)
    c: Coincident(g11,g-3)
    c: Equal(g11,g10)
    c: Coincident(g12,g1)
    c: Coincident(g12,g0)
    c: Coincident(g13,g3)
    c: Coincident(g13,g4)
    c: Horizontal(g13)
    c: Horizontal(g12)
    c: PointOnObject(g6,g12)
    c: Radius(g6) = 0.75
    c: Distance(g5,g2) = 4
    c: DistanceY(g2,g2) = 7
    c: DistanceX(g1,g1) = 0.5
FEATURE [PartDesign::Pocket] Pocket008
  BaseFeature = -> Pad007
  Direction = (0,-1,2e-16)
  Length = 5
  Length2 = 5
  Profile = -> Sketch011
  ReferenceAxis = -> Sketch011 [N_Axis]
  Refine = true
  SideType = 0
  Suppressed = false
  Type = 3
  Type2 = 0
  UpToFace = -> Pad007 [Face54]
FEATURE [PartDesign::Body] Body002  label="Rack"
  AllowCompound = false
  Group = -> [InvoluteRack,Sketch009,Pad006,Sketch010,Pad007,Sketch011,Pocket008]
  Origin = -> Origin008
  Placement = pos=(-5,-1.5,7.5) rot=(0,0,1;0rad)
  Tip = -> Pocket008
FEATURE [App::Link] Jaw_Shell_Bottom  label="Jaw_Shell_Bottom001"
  LinkedObject = -> Body
FEATURE [App::Link] Rail  label="Rail001"
  LinkPlacement = pos=(15.125,-35,16.125) rot=(0.57735,0.57735,-0.57735;4.18879rad)
  LinkedObject = -> Body004
  Placement = pos=(15.125,-35,16.125) rot=(0.57735,0.57735,-0.57735;4.18879rad)
FEATURE [App::Link] Shaft  label="Shaft001"
  LinkPlacement = pos=(0,5.60683e-06,33) rot=(1,0,0;3.14159rad)
  LinkedObject = -> Body003
  Placement = pos=(0,5.60683e-06,33) rot=(1,0,0;3.14159rad)
FEATURE [App::Link] Rail001  label="Rail002"
  LinkPlacement = pos=(-14.875,-35.5,9.12501) rot=(0.57735,0.57735,0.57735;2.0944rad)
  LinkedObject = -> Body004
  Placement = pos=(-14.875,-35.5,9.12501) rot=(0.57735,0.57735,0.57735;2.0944rad)
FEATURE [App::Link] Rack  label="Rack001"
  LinkPlacement = pos=(-4.85,-1.6,7.61) rot=(0,0,1;0rad)
  LinkedObject = -> Body002
  Placement = pos=(-4.85,-1.6,7.61) rot=(0,0,1;0rad)
FEATURE [App::Link] Rack001  label="Rack002"
  LinkPlacement = pos=(5.12624,1.58,7.63) rot=(0,0,-1;3.14159rad)
  LinkedObject = -> Body002
  Placement = pos=(5.12624,1.58,7.63) rot=(0,0,-1;3.14159rad)
FEATURE [App::FeaturePython] GroundedJoint  label="GroundedJoint001"  # Assembly grounded joint (typed FeaturePython)
  ObjectToGround = -> Jaw_Shell_Bottom
FEATURE [Assembly::JointGroup] Joints
  Group = -> [GroundedJoint]
FEATURE [App::Link] Jaw_Shell_Top  label="Jaw_Shell_Top001"
  LinkPlacement = pos=(1.19209e-06,-7.12879e-06,84) rot=(0.707107,0.707107,0;3.14159rad)
  LinkedObject = -> Body001
  Placement = pos=(1.19209e-06,-7.12879e-06,84) rot=(0.707107,0.707107,0;3.14159rad)
FEATURE [Assembly::AssemblyObject] Assembly
  Group = -> [Joints,Shaft,Jaw_Shell_Bottom,Rail,Rail001,Rack,Rack001,GroundedJoint,Jaw_Shell_Top]
  Origin = -> Origin
  Type = Assembly
FEATURE [Sketcher::SketchObject] Sketch014
  ArcFitTolerance = 1e-06
  AttachmentSupport = -> [Pocket004]
  ExternalTypes = [0]
  FullyConstrained = true
  MakeInternals = false
  MapMode = 5
  Placement = pos=(0,0,0) rot=(1,0,0;3.14159rad)
  _ExternalGeoVersion = 1
  sketch-geometry (24):
    g0: LineSegment StartX=3.5 StartY=34 StartZ=0 EndX=3.5 EndY=8 EndZ=0
    g1: LineSegment StartX=3.5 StartY=8 StartZ=0 EndX=9 EndY=8 EndZ=0
    g2: LineSegment StartX=9 StartY=8 StartZ=0 EndX=9 EndY=34 EndZ=0
    g3: LineSegment StartX=9 StartY=34 StartZ=0 EndX=3.5 EndY=34 EndZ=0
    g4: LineSegment StartX=8 StartY=-3.5 StartZ=0 EndX=8 EndY=-9 EndZ=0
    g5: LineSegment StartX=8 StartY=-9 StartZ=0 EndX=34 EndY=-9 EndZ=0
    g6: LineSegment StartX=34 StartY=-9 StartZ=0 EndX=34 EndY=-3.5 EndZ=0
    g7: LineSegment StartX=34 StartY=-3.5 StartZ=0 EndX=8 EndY=-3.5 EndZ=0
    g8: LineSegment StartX=-9 StartY=-8 StartZ=0 EndX=-9 EndY=-34 EndZ=0
    g9: LineSegment StartX=-9 StartY=-34 StartZ=0 EndX=-3.5 EndY=-34 EndZ=0
    g10: LineSegment StartX=-3.5 StartY=-34 StartZ=0 EndX=-3.5 EndY=-8 EndZ=0
    g11: LineSegment StartX=-3.5 StartY=-8 StartZ=0 EndX=-9 EndY=-8 EndZ=0
    g12: LineSegment StartX=-8 StartY=9 StartZ=0 EndX=-34 EndY=9 EndZ=0
    g13: LineSegment StartX=-34 StartY=9 StartZ=0 EndX=-34 EndY=3.5 EndZ=0
    g14: LineSegment StartX=-34 StartY=3.5 StartZ=0 EndX=-8 EndY=3.5 EndZ=0
    g15: LineSegment StartX=-8 StartY=3.5 StartZ=0 EndX=-8 EndY=9 EndZ=0
    g16: LineSegment [constr] StartX=3.5 StartY=0 StartZ=0 EndX=3.5 EndY=8 EndZ=0
    g17: LineSegment [constr] StartX=0 StartY=8 StartZ=0 EndX=3.5 EndY=8 EndZ=0
    g18: LineSegment [constr] StartX=-8 StartY=0 StartZ=0 EndX=-8 EndY=3.5 EndZ=0
    g19: LineSegment [constr] StartX=-8 StartY=3.5 StartZ=0 EndX=0 EndY=3.5 EndZ=0
    g20: LineSegment [constr] StartX=0 StartY=-8 StartZ=0 EndX=-3.5 EndY=-8 EndZ=0
    g21: LineSegment [constr] StartX=-3.5 StartY=-8 StartZ=0 EndX=-3.5 EndY=0 EndZ=0
    g22: LineSegment [constr] StartX=0 StartY=-3.5 StartZ=0 EndX=8 EndY=-3.5 EndZ=0
    g23: LineSegment [constr] StartX=8 StartY=0 StartZ=0 EndX=8 EndY=-3.5 EndZ=0
  constraints (72):
    c: Coincident(g0,g1)
    c: Coincident(g1,g2)
    c: Coincident(g2,g3)
    c: Coincident(g3,g0)
    c: Vertical(g0)
    c: Vertical(g2)
    c: Horizontal(g1)
    c: Horizontal(g3)
    c: Coincident(g4,g5)
    c: Coincident(g5,g6)
    c: Coincident(g6,g7)
    c: Coincident(g7,g4)
    c: Vertical(g4)
    c: Vertical(g6)
    c: Horizontal(g5)
    c: Horizontal(g7)
    c: Distance(g4,g6) = 26
    c: Distance(g5,g7) = 5.5
    c: Coincident(g8,g9)
    c: Coincident(g9,g10)
    c: Coincident(g10,g11)
    c: Coincident(g11,g8)
    c: Vertical(g8)
    c: Vertical(g10)
    c: Horizontal(g9)
    c: Horizontal(g11)
    c: Coincident(g12,g13)
    c: Coincident(g13,g14)
    c: Coincident(g14,g15)
    c: Coincident(g15,g12)
    c: Horizontal(g12)
    c: Horizontal(g14)
    c: Vertical(g13)
    c: Vertical(g15)
    c: Distance(g-1,g7) = 3.5
    c: Equal(g5,g2)
    c: Equal(g5,g14)
    c: Equal(g5,g8)
    c: PointOnObject(g16,g-1)
    c: Coincident(g16,g0)
    c: PointOnObject(g17,g-2)
    c: Coincident(g17,g0)
    c: PointOnObject(g18,g-1)
    c: Coincident(g18,g14)
    c: Coincident(g19,g14)
    c: PointOnObject(g19,g-2)
    c: Horizontal(g19)
    c: PointOnObject(g20,g-2)
    c: Coincident(g20,g10)
    c: Coincident(g21,g10)
    c: PointOnObject(g21,g-1)
    c: PointOnObject(g22,g-2)
    c: Coincident(g22,g4)
    c: PointOnObject(g23,g-1)
    c: Coincident(g23,g4)
    c: Horizontal(g17)
    c: Horizontal(g22)
    c: Horizontal(g20)
    c: Vertical(g21)
    c: Vertical(g18)
    c: Vertical(g23)
    c: Vertical(g16)
    c: Distance(g-2,g4) = 8
    c: Equal(g22,g16)
    c: Equal(g22,g19)
    c: Equal(g22,g21)
    c: Equal(g23,g17)
    c: Equal(g23,g18)
    c: Equal(g23,g20)
    c: Equal(g4,g1)
    c: Equal(g4,g11)
    c: Equal(g4,g15)
FEATURE [PartDesign::Pocket] Pocket009
  BaseFeature = -> Pocket005
  Direction = (0,0,1)
  Length = 5
  Length2 = 5
  Profile = -> Sketch014
  ReferenceAxis = -> Sketch014 [N_Axis]
  Refine = true
  SideType = 0
  Suppressed = false
  Type = 1
  Type2 = 0
FEATURE [PartDesign::Body] Body001  label="Jaw_Shell_Top"
  AllowCompound = true
  Group = -> [Sketch004,Pad001,DatumPlane001,Sketch005,Pocket003,Sketch006,Pocket004,Sketch007,Pocket005,Sketch014,Pocket009]
  Origin = -> Origin006
  Placement = pos=(-3.8e-15,3.8e-15,83) rot=(0.707107,0.707107,0;3.14159rad)
  Tip = -> Pocket009
FEATURE [Sketcher::SketchObject] Sketch015
  ArcFitTolerance = 1e-06
  AttachmentSupport = -> [Pocket002]
  ExternalGeometry = -> [Pocket002]
  ExternalTypes = [0,0]
  FullyConstrained = true
  MakeInternals = false
  MapMode = 5
  Placement = pos=(-15,0,0) rot=(0.57735,0.57735,0.57735;2.0944rad)
  _ExternalGeoVersion = 1
  sketch-geometry (9):
    g0: Circle CenterX=22.5 CenterY=12.25 CenterZ=0 NormalX=0 NormalY=0 NormalZ=1 AngleXU=0 Radius=2
    g1: Circle CenterX=-22.5 CenterY=12.25 CenterZ=0 NormalX=0 NormalY=0 NormalZ=1 AngleXU=0 Radius=2
    g2: Circle CenterX=-7.5 CenterY=12.25 CenterZ=0 NormalX=0 NormalY=0 NormalZ=1 AngleXU=0 Radius=2
    g3: Circle CenterX=7.5 CenterY=12.25 CenterZ=0 NormalX=0 NormalY=0 NormalZ=1 AngleXU=0 Radius=2
    g4: LineSegment [constr] StartX=22.5 StartY=12.25 StartZ=0 EndX=7.5 EndY=12.25 EndZ=0
    g5: LineSegment [constr] StartX=7.5 StartY=12.25 StartZ=0 EndX=-7.5 EndY=12.25 EndZ=0
    g6: LineSegment [constr] StartX=-7.5 StartY=12.25 StartZ=0 EndX=-22.5 EndY=12.25 EndZ=0
    g7: LineSegment [constr] StartX=-22.5 StartY=12.25 StartZ=0 EndX=-37.081 EndY=12.25 EndZ=0
    g8: LineSegment [constr] StartX=22.5 StartY=12.25 StartZ=0 EndX=37.081 EndY=12.25 EndZ=0
  constraints (23):
    c: Diameter(g1) = 4
    c: Coincident(g0,g4)
    c: Coincident(g4,g3)
    c: Coincident(g4,g5)
    c: Coincident(g5,g2)
    c: Coincident(g5,g6)
    c: Coincident(g6,g1)
    c: Coincident(g6,g7)
    c: Horizontal(g7)
    c: Horizontal(g5)
    c: Horizontal(g6)
    c: Horizontal(g4)
    c: Equal(g1,g2)
    c: Equal(g1,g3)
    c: Equal(g1,g0)
    c: Equal(g6,g5)
    c: Equal(g6,g4)
    c: Equal(g8,g7)
    c: Horizontal(g8)
    c: PointOnObject(g7,g-4)
    c: Symmetric(g-3,g-3,g8)
    c: Coincident(g0,g8)
    c: DistanceX(g5,g5) = 15
FEATURE [Sketcher::SketchObject] Sketch016
  ArcFitTolerance = 1e-06
  AttachmentSupport = -> [Pocket002]
  ExternalGeometry = -> [Pocket002]
  ExternalTypes = [0,0]
  FullyConstrained = true
  MakeInternals = false
  MapMode = 5
  Placement = pos=(15,0,0) rot=(0.57735,-0.57735,-0.57735;2.0944rad)
  _ExternalGeoVersion = 1
  sketch-geometry (9):
    g0: Circle CenterX=22.5 CenterY=12.25 CenterZ=0 NormalX=0 NormalY=0 NormalZ=1 AngleXU=0 Radius=2
    g1: Circle CenterX=-22.5 CenterY=12.25 CenterZ=0 NormalX=0 NormalY=0 NormalZ=1 AngleXU=0 Radius=2
    g2: Circle CenterX=-7.5 CenterY=12.25 CenterZ=0 NormalX=0 NormalY=0 NormalZ=1 AngleXU=0 Radius=2
    g3: Circle CenterX=7.5 CenterY=12.25 CenterZ=0 NormalX=0 NormalY=0 NormalZ=1 AngleXU=0 Radius=2
    g4: LineSegment [constr] StartX=22.5 StartY=12.25 StartZ=0 EndX=7.5 EndY=12.25 EndZ=0
    g5: LineSegment [constr] StartX=7.5 StartY=12.25 StartZ=0 EndX=-7.5 EndY=12.25 EndZ=0
    g6: LineSegment [constr] StartX=-7.5 StartY=12.25 StartZ=0 EndX=-22.5 EndY=12.25 EndZ=0
    g7: LineSegment [constr] StartX=-22.5 StartY=12.25 StartZ=0 EndX=-37.081 EndY=12.25 EndZ=0
    g8: LineSegment [constr] StartX=22.5 StartY=12.25 StartZ=0 EndX=37.081 EndY=12.25 EndZ=0
  constraints (22):
    c: Diameter(g1) = 4
    c: Coincident(g0,g4)
    c: Coincident(g4,g3)
    c: Coincident(g4,g5)
    c: Coincident(g5,g2)
    c: Coincident(g5,g6)
    c: Coincident(g6,g1)
    c: Coincident(g6,g7)
    c: Horizontal(g7)
    c: Horizontal(g5)
    c: Horizontal(g6)
    c: Horizontal(g4)
    c: Equal(g1,g2)
    c: Equal(g1,g3)
    c: Equal(g1,g0)
    c: Equal(g6,g5)
    c: Equal(g6,g4)
    c: Equal(g8,g7)
    c: Symmetric(g-4,g-4,g8)
    c: Symmetric(g-3,g-3,g7)
    c: Coincident(g8,g0)
    c: DistanceX(g5,g5) = 15
FEATURE [PartDesign::Pocket] Pocket010
  BaseFeature = -> Pocket002
  Direction = (-1,0,0)
  Length = 5
  Length2 = 5
  Profile = -> Sketch015
  ReferenceAxis = -> Sketch015 [N_Axis]
  Refine = true
  SideType = 0
  Suppressed = false
  Type = 0
  Type2 = 0
FEATURE [PartDesign::Pocket] Pocket011
  BaseFeature = -> Pocket010
  Direction = (1,0,0)
  Length = 5
  Length2 = 5
  Profile = -> Sketch016
  ReferenceAxis = -> Sketch016 [N_Axis]
  Refine = true
  SideType = 0
  Suppressed = false
  Type = 0
  Type2 = 0
FEATURE [PartDesign::Body] Body  label="Jaw_Shell_Bottom"
  AllowCompound = true
  Group = -> [Sketch,Pad,DatumPlane,Sketch001,Pocket,Sketch002,Pocket001,Sketch003,Pocket002,Sketch015,Sketch016,Pocket010,Pocket011]
  Origin = -> Origin004
  Tip = -> Pocket011
